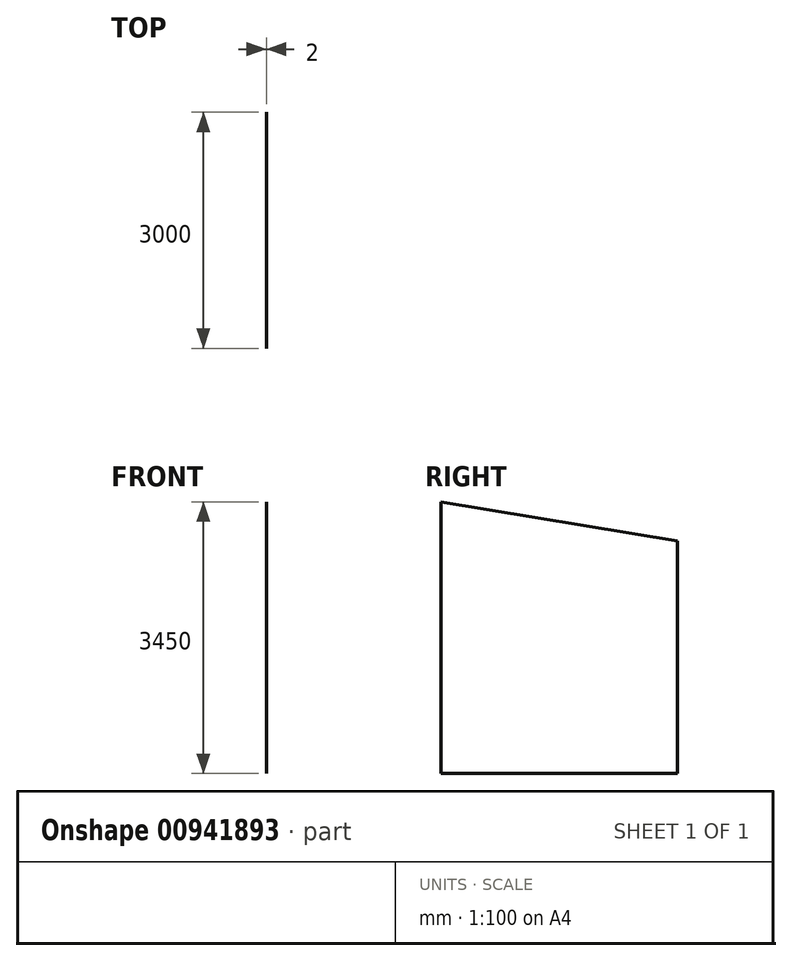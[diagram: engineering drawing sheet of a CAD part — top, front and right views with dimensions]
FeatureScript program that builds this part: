
annotation { "Feature Type Name" : "Feature", "Feature Type Description" : "" }
export const myFeature = defineFeature(function(context is Context, id is Id, definition is map)
    precondition{}
    {
        {
            var Q0;
            Q0=qCreatedBy(makeId("Right.planeOp"),FACE);
            var sketch = newSketch(context, id + "F0", { "sketchPlane" : qUnion([Q0])});
            skLineSegment(sketch, "E0", {"start": v(0, 0) * mm, "end": v(0, 3450) * mm});
            skLineSegment(sketch, "E1", {"start": v(0, 0) * mm, "end": v(3000, 0) * mm});
            skLineSegment(sketch, "E2", {"start": v(3000, 0) * mm, "end": v(3000, 2950) * mm});
            skLineSegment(sketch, "E3", {"start": v(3000, 2950) * mm, "end": v(0, 3450) * mm});
            skSolve(sketch);
        }
        {
            var Q0;
            Q0=makeQuery(id+"F0.imprint","IMPRINT",FACE,{"disambiguationData":[TD([[makeQuery(id+"F0.imprint","IMPRINT",EDGE,{"derivedFrom":sQuery(id+"F0.wireOp",EDGE,"E0")}),-1.0]])]});
            extrude(context, id + "F1", {"entities" : qUnion([Q0]), "depth" : 2 * mm, "offsetDistance" : 25 * mm});
        }
    });
